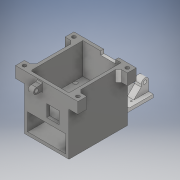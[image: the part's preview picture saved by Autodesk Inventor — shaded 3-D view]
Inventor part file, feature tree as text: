
AUTODESK INVENTOR PART (.ipt)
format: ipt  version: 2018 (Build 220112000, 112)  size: 1,372,672 bytes
history: native  units: in
note: dims shown in document units (in); Inventor stores cm internally (conversion verified against a paired STEP export)
features: sketch x43, extrude x40, move_body x18, direct_edit x15, chamfer x8, fillet x6, thicken_offset x3, delete_face x2, projected_geometry x2
ambient origin geometry x8: Origin, YZ Plane, XZ Plane, XY Plane, X Axis, Y Axis, Z Axis, Center Point
bodies: Solid1 (feature_tree)
feature tree (137):
  extrude  "Extrusion1"  Depth=0.125in
  extrude  "Extrusion2"  Depth=2.2in TaperAngle=0.0deg
  extrude  "Extrusion3"  Depth=0.125in
  extrude  "Extrusion4"  Depth=0.0625in
  sketch  "Sketch6"  dims[d11=0.5in d13=0.55in]
  extrude  "Extrusion6"  Depth=0.55in
  extrude  "Extrusion7"  Depth=0.725in
  extrude  "Extrusion8"  Depth=0.09in
  extrude  "Extrusion9"  Depth=0.125in
  extrude  "Extrusion10"  Depth=0.125in TaperAngle=0.0deg
  extrude  "Extrusion11"  Depth=0.7in
  extrude  "Extrusion12"  Depth=0.5in
  sketch  "Sketch16"  dims[d38=0.05in]
  extrude  "Extrusion13"  Depth=0.05in
  sketch  "Sketch18"  dims[d40=0.45in]
  fillet  "Fillet1"  Radius=0.05in
  chamfer  "Chamfer1"  Distance=0.36in
  chamfer  "Chamfer2"  Distance=0.25in
  extrude  "Extrusion14"  Depth=0.05in
  extrude  "Extrusion15"  Depth=0.35in
  extrude  "Extrusion16"  Depth=0.25in
  fillet  "Fillet2"  Radius=0.25in
  extrude  "Extrusion17"  Depth=0.1in
  chamfer  "Chamfer3"  Distance=0.05in Angle=45.0deg
  extrude  "Extrusion18"  Depth=0.125in
  extrude  "Extrusion19"  Depth=0.05in TaperAngle=0.0deg
  extrude  "Extrusion20"  Depth=0.05in
  extrude  "Extrusion21"  Depth=0.1in
  fillet  "Fillet3"  Radius=0.275in
  fillet  "Fillet4"  Radius=0.36in
  extrude  "Extrusion22"  Depth=0.225in
  extrude  "Extrusion23"  Depth=0.26in TaperAngle=0.0deg
  chamfer  "Chamfer4"  Distance=0.05in
  chamfer  "Chamfer5"  Distance=0.05in Angle=45.0deg
  extrude  "Extrusion24"  Depth=0.05in TaperAngle=0.0deg
  extrude  "Extrusion25"  Depth=0.125in TaperAngle=0.0deg
  extrude  "Extrusion28"  Depth=1.0in
  extrude  "Extrusion29"  Depth=1.0in
  extrude  "Extrusion30"  Depth=0.25in
  extrude  "Extrusion31"  Depth=0.25in
  thicken_offset  "Thicken1"
  thicken_offset  "Thicken2"
  thicken_offset  "Thicken3"
  direct_edit  "Direct Edit1"
  direct_edit  "Direct Edit2"
  direct_edit  "Direct Edit3"
  direct_edit  "Direct Edit4"
  extrude  "Extrusion32"  Depth=0.21in TaperAngle=0.0deg
  fillet  "Fillet5"  Radius=0.5in
  chamfer  "Chamfer7"  Distance=0.63in
  direct_edit  "Direct Edit5"
  direct_edit  "Direct Edit6"
  extrude  "Extrusion33"  Depth=0.25in
  extrude  "Extrusion34"  Depth=0.25in
  extrude  "Extrusion35"  Depth=0.25in
  direct_edit  "Direct Edit7"
  extrude  "Extrusion36"  Depth=0.25in
  direct_edit  "Direct Edit8"
  delete_face  "Delete Face1"
  direct_edit  "Direct Edit9"
  direct_edit  "Direct Edit10"
  extrude  "Extrusion37"  Depth=0.25in
  extrude  "Extrusion38"  Depth=0.25in
  fillet  "Fillet6"  Radius=0.437in
  extrude  "Extrusion39"  Depth=0.1in TaperAngle=0.0deg
  chamfer  "Chamfer9"  Distance=0.344in
  extrude  "Extrusion40"  Depth=0.25in
  extrude  "Extrusion41"  Depth=0.25in
  chamfer  "Chamfer10"  Distance=0.344in
  extrude  "Extrusion42"  Depth=0.1in TaperAngle=0.0deg
  extrude  "Extrusion43"  Depth=0.1in TaperAngle=45.0deg
  direct_edit  "Direct Edit11"
  direct_edit  "Direct Edit12"
  delete_face  "Delete Face2"
  direct_edit  "Direct Edit13"
  direct_edit  "Direct Edit14"
  direct_edit  "Direct Edit15"
  sketch  "Sketch1"  dims[d0=0.125in d1=1.24in]
  sketch  "Sketch2"  dims[d2=0.9in d3=2.2in d4=0.0in]
  sketch  "Sketch3"  dims[d5=0.125in d6=0.0in d7=2.0in]
  sketch  "Sketch4"  dims[d8=0.125in d9=0.0in d10=0.0625in]
  sketch  "Sketch8"  dims[d14=0.125in d15=0.0in d16=0.725in]
  sketch  "Sketch10"  dims[d17=2.06in d21=0.09in]
  sketch  "Sketch11"  dims[d22=0.4in d23=0.0in d24=0.125in]
  sketch  "Sketch12"  dims[d25=1.475in d26=0.0in d27=0.125in d28=0.0in]
  sketch  "Sketch13"  dims[d29=0.6in d30=0.7in]
  sketch  "Sketch14"  dims[d31=0.5in d32=0.0in d33=0.1603in]
  sketch  "Sketch15"  dims[d34=0.5in d35=0.0in d36=0.146in d37=0.05in]
  sketch  "Sketch17"  dims[d39=0.1in]
  sketch  "Sketch19"  dims[d41=1.0in d42=0.36in d43=0.0in]
  sketch  "Sketch20"  dims[d44=0.225in]
  sketch  "Sketch21"  dims[d45=0.146in d46=0.25in d47=0.0in]
  sketch  "Sketch22"  dims[d49=0.05in d50=0.0in d51=0.05in]
  sketch  "Sketch24"  dims[d52=0.05in d53=0.35in]
  sketch  "Sketch25"  dims[d54=0.02in d55=0.02in d56=0.25in]
  sketch  "Sketch26"  dims[d57=0.25in d58=0.1in]
  sketch  "Sketch27"  dims[d59=0.0in]
  sketch  "Sketch28"  dims[d60=0.35in]
  sketch  "Sketch29"  dims[d61=0.346in]
  sketch  "Sketch30"  dims[d62=0.425in]
  sketch  "Sketch31"  dims[d63=0.9in]
  sketch  "Sketch34"  dims[d64=0.123in]
  sketch  "Sketch35"  dims[d65=0.123in d66=0.05in d67=0.125in d68=45.0deg]
  sketch  "Sketch36"  dims[d69=0.05in d70=0.125in d71=45.0deg d72=0.01in]
  sketch  "Sketch37"  dims[d73=0.4in d74=0.05in d75=0.0in]
  projected_geometry  "Projected Loop1"
  sketch  "Sketch38"  dims[d76=0.146in d77=0.05in]
  sketch  "Sketch39"  dims[d78=0.05in d80=0.1in d81=0.275in d82=0.36in d83=0.0in]
  sketch  "Sketch40"  dims[d84=0.225in d85=0.01in]
  sketch  "Sketch41"  dims[d86=0.146in d87=0.26in d88=0.0in]
  sketch  "Sketch42"  dims[d89=0.123in]
  sketch  "Sketch43"  dims[d90=0.05in]
  sketch  "Sketch44"  dims[d91=0.05in d92=0.05in d93=0.0in d94=0.05in d95=0.125in d96=45.0deg]
  sketch  "Sketch45"  dims[d97=0.45in d98=0.05in d99=0.0in]
  sketch  "Sketch46"  dims[d100=0.125in d101=0.0in d102=0.125in d103=0.0in]
  sketch  "Sketch47"  dims[d104=1.0in d105=1.0in]
  projected_geometry  "Projected Loop2"
  sketch  "Sketch48"  dims[d106=1.0in d107=0.912in]
  sketch  "Sketch49"  dims[d108=0.912in d109=0.912in d110=0.912in d111=0.21in d112=0.0in d113=0.5in d114=0.63in d115=0.63in d116=0.63in d117=0.63in d118=0.437in d119=0.437in d120=0.437in d121=0.437in d122=0.1in d123=0.0in d124=0.344in d125=0.344in d126=0.344in d127=0.344in d128=0.1in d129=0.0in d130=0.1in d131=0.125in d132=45.0deg d133=0.05in d134=0.125in d135=45.0deg d139=0.312in d140=0.3603in d141=0.3603in d142=0.3603in d143=0.3603in d144=0.3603in d145=0.45in d146=0.0in d147=0.146in d148=0.146in d149=0.146in d150=0.146in d151=0.5in d152=0.0in d163=1.0in d164=0.0in d165=0.35in d166=1.5in d168=0.3in d169=1.0in d170=0.0in d171=0.05in d172=0.3in d173=0.0in d174=0.05in d175=0.0in d176=0.1in d177=0.1in d178=0.1in d179=0.1in d180=0.1in d181=0.1in d182=0.0in d183=0.0in d184=0.1in d185=0.0in d186=0.0in d187=-0.1in d188=0.0in d189=0.0in d190=-0.05in d191=0.5in d192=0.0in d193=0.0in d194=0.05in d195=0.937in d196=0.937in d197=0.937in d198=0.937in d199=0.375in d200=0.0in d201=0.5in d202=0.125in d203=0.125in d204=45.0deg d205=0.0in d206=0.0in d207=-0.175in d208=0.0in d209=0.0in d210=0.35in d211=0.0in d212=0.0in d213=0.105in d214=0.0in d215=0.0in d216=0.105in d217=0.16in d218=1.0in d219=0.0in d220=3.9056in d221=0.6in d222=0.0in d223=0.0in d224=3.9in d225=0.6in d226=1.0in d227=0.0in d228=0.0in d229=0.0in d230=0.2in d231=0.0in d232=0.0in d233=0.0in d234=0.0in d235=0.7in d236=0.0in d237=0.0in d238=-0.065in d239=0.0in d240=0.0in d241=-1.54in d242=0.125in d243=0.9in d244=1.5in d245=0.0in d249=0.26in d250=0.3in d251=0.19in d252=0.55in d253=0.0in d254=0.15in d255=0.146in d256=0.36in d257=0.0in d258=0.3in d259=0.125in d260=45.0deg d261=0.1in d262=0.0in d263=0.1in d264=0.0in d265=0.1in d266=0.125in d267=45.0deg d268=0.6in d269=0.15in d270=0.0in d271=0.1in d272=0.0in d273=0.06in d274=0.06in d275=0.25in d276=0.25in d277=0.1in d278=0.0in d279=45.0deg d280=0.75in d281=0.2in d282=0.0in d283=0.0in d284=0.0in d285=0.0in d286=0.02in d287=0.0in d288=0.0in d289=0.09in d290=0.25in d291=0.0in d292=0.0in d293=0.0in d294=0.3in d295=0.0in d296=0.25in d297=0.0in d298=0.0in]
  move_body  "Move1"
  move_body  "Move2"
  move_body  "Move3"
  move_body  "Move4"
  move_body  "Move5"
  move_body  "Move6"
  move_body  "Move7"
  move_body  "Move8"
  move_body  "Move9"
  move_body  "Move10"
  move_body  "Move11"
  move_body  "Move12"
  move_body  "Move13"
  move_body  "Move14"
  move_body  "Move15"
  move_body  "Move16"
  move_body  "Move17"
  move_body  "Move18"
